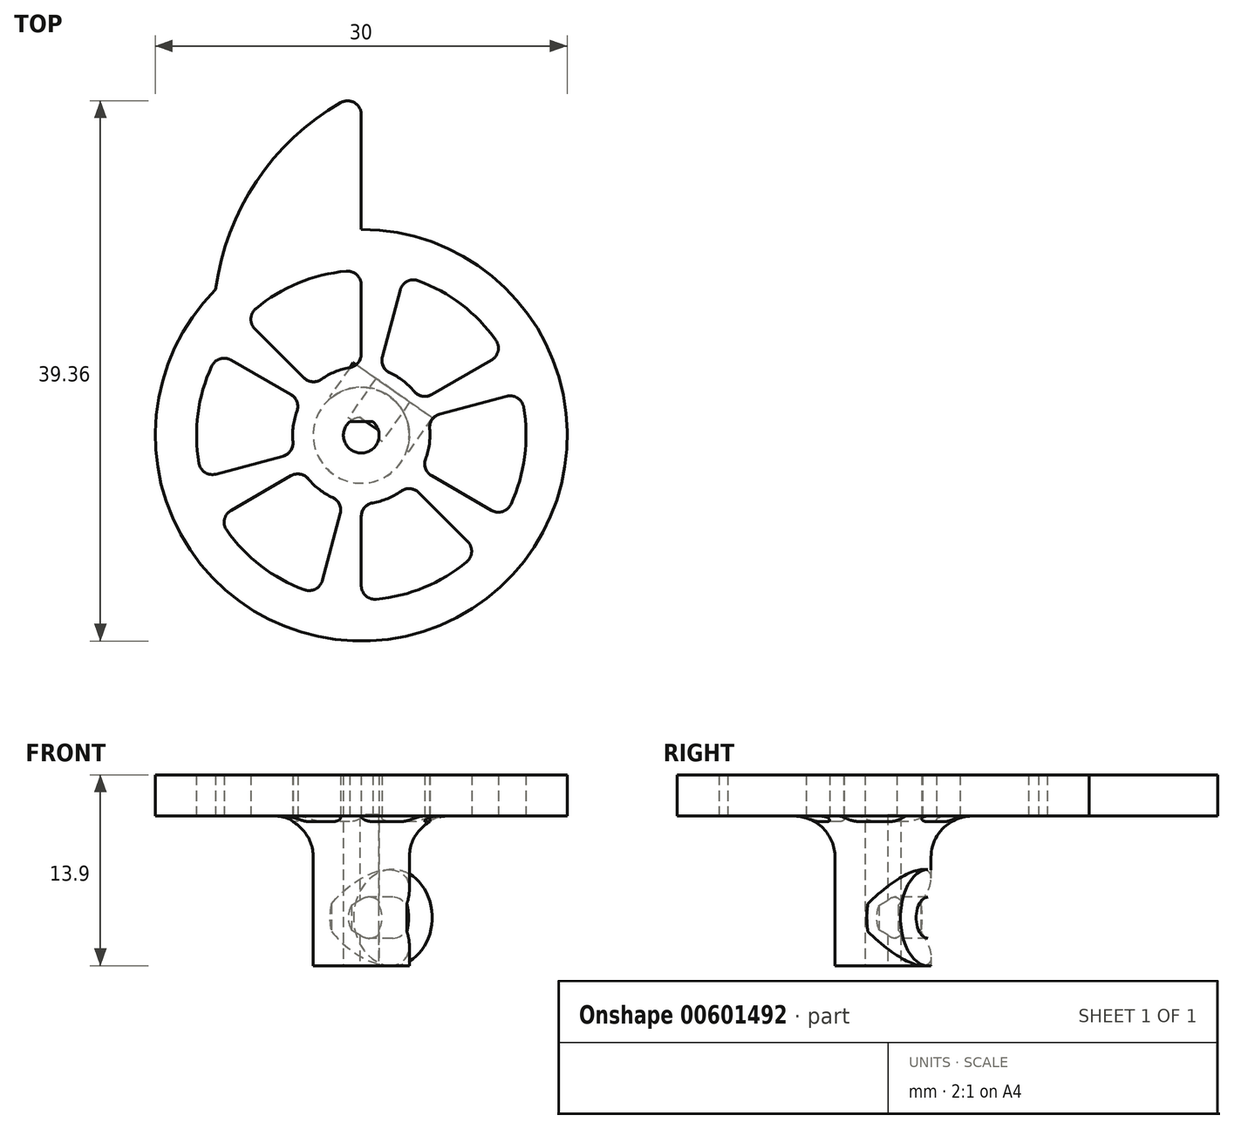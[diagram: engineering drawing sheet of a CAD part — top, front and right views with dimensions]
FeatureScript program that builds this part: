
annotation { "Feature Type Name" : "Feature", "Feature Type Description" : "" }
export const myFeature = defineFeature(function(context is Context, id is Id, definition is map)
    precondition{}
    {
        {
            assignVariable(context, id + "F0", {"name" : "shaftL", "anyValue" : 11});
        }
        {
            assignVariable(context, id + "F1", {"name" : "wheelThickness", "anyValue" : 3});
        }
        {
            var Q0;
            Q0=qCreatedBy(makeId("Top.planeOp"),FACE);
            var sketch = newSketch(context, id + "F2", { "sketchPlane" : qUnion([Q0])});
            skCircle(sketch, "E0", {"center": v(0, 0) * mm, "radius": 1.3 * mm});
            skLineSegment(sketch, "E1", {"start": v(0, 0) * mm, "end": v(0, 1) * mm, "construction": true});
            skLineSegment(sketch, "E2", {"start": v(0, 1) * mm, "end": v(0.83, 1) * mm});
            skLineSegment(sketch, "E3", {"start": v(0, 1) * mm, "end": v(-0.83, 1) * mm});
            skCircle(sketch, "E4", {"center": v(0, 0) * mm, "radius": 3.5 * mm});
            skSolve(sketch);
        }
        {
            var Q0;
            Q0=makeQuery(id+"F2.imprint","IMPRINT",FACE,{"disambiguationData":[TD([[makeQuery(id+"F2.imprint","IMPRINT",EDGE,{"derivedFrom":sQuery(id+"F2.wireOp",EDGE,"E4")}),1.0]])]});
            var Q1;
            {var subQ0=sQuery(id+"F2.wireOp",EDGE,"E2");Q1=makeQuery(id+"F2.imprint","IMPRINT",FACE,{"disambiguationData":[TD([[makeQuery(id+"F2.imprint","IMPRINT",EDGE,{"derivedFrom":subQ0}),1.0]])]});}
            extrude(context, id + "F3", {"entities" : qUnion([Q0, Q1]), "depth" : (getVariable(context, 'shaftL')) * mm, "offsetDistance" : 25 * mm});
        }
        {
            var Q0;
            Q0=makeQuery(id+"F3.opExtrude","SWEPT_FACE",FACE,{"disambiguationData":[OSD([sQuery(id+"F2.wireOp",EDGE,"E2"),sQuery(id+"F2.wireOp",EDGE,"E3")])]});
            var sketch = newSketch(context, id + "F4", { "sketchPlane" : qUnion([Q0])});
            skLineSegment(sketch, "E5", {"start": v(0, 0) * mm, "end": v(0, 11) * mm, "construction": true});
            skCircle(sketch, "E6", {"center": v(0, 3.5) * mm, "radius": 1.5 * mm});
            skCircle(sketch, "E7", {"center": v(0, 3.5) * mm, "radius": 3.5 * mm});
            skSolve(sketch);
        }
        {
            var Q0;
            {var subQ0=sQuery(id+"F4.wireOp",EDGE,"E6");var subQ1=sQuery(id+"F2.wireOp",EDGE,"E0");var subQ2=makeQuery(id+"F3.opExtrude","SWEPT_EDGE",EDGE,{"disambiguationData":[OSD([subQ1,sQuery(id+"F2.wireOp",EDGE,"E3")])]});var subQ3=makeQuery(id+"F4.imprint","INTERSECT",VERTEX,{"disambiguationData":[OD(0.0)],"derivedFrom":[subQ2,subQ0]});Q0=makeQuery(id+"F4.imprint","IMPRINT",FACE,{"disambiguationData":[TD([[makeQuery(id+"F4.imprint","IMPRINT",EDGE,{"disambiguationData":[TD([[subQ3,1.0]])],"derivedFrom":subQ0}),1.0]])]});}
            var Q1;
            {var subQ0=sQuery(id+"F4.wireOp",EDGE,"E6");var subQ1=makeQuery(id+"F3.opExtrude","SWEPT_EDGE",EDGE,{"disambiguationData":[OSD([sQuery(id+"F2.wireOp",EDGE,"E0"),sQuery(id+"F2.wireOp",EDGE,"E2")])]});var subQ2=makeQuery(id+"F4.imprint","INTERSECT",VERTEX,{"disambiguationData":[OD(0.0)],"derivedFrom":[subQ1,subQ0]});Q1=makeQuery(id+"F4.imprint","IMPRINT",FACE,{"disambiguationData":[TD([[makeQuery(id+"F4.imprint","IMPRINT",EDGE,{"disambiguationData":[TD([[subQ2,1.0]])],"derivedFrom":subQ0}),1.0]])]});}
            var Q2;
            {var subQ0=sQuery(id+"F4.wireOp",EDGE,"E6");var subQ1=makeQuery(id+"F3.opExtrude","SWEPT_EDGE",EDGE,{"disambiguationData":[OSD([sQuery(id+"F2.wireOp",EDGE,"E0"),sQuery(id+"F2.wireOp",EDGE,"E3")])]});var subQ2=makeQuery(id+"F4.imprint","INTERSECT",VERTEX,{"disambiguationData":[OD(0.0)],"derivedFrom":[subQ1,subQ0]});Q2=makeQuery(id+"F4.imprint","IMPRINT",FACE,{"disambiguationData":[TD([[makeQuery(id+"F4.imprint","IMPRINT",EDGE,{"disambiguationData":[TD([[subQ2,-1.0]])],"derivedFrom":subQ0}),1.0]])]});}
            var Q3;
            Q3=sQuery(id+"F4.wireOp",EDGE,"E6");
            extrude(context, id + "F5", {"entities" : qUnion([Q0, Q1, Q2]), "operationType" : NewBodyOperationType.REMOVE, "surfaceEntities" : qUnion([Q3]), "oppositeDirection" : true, "depth" : 25 * mm, "offsetDistance" : 25 * mm, "hasSecondDirection" : true, "secondDirectionOppositeDirection" : false, "secondDirectionDepth" : 0.5 * mm});
        }
        {
            var Q0;
            {var subQ0=sQuery(id+"F4.wireOp",EDGE,"E6");var subQ1=makeQuery(id+"F3.opExtrude","SWEPT_EDGE",EDGE,{"disambiguationData":[OSD([sQuery(id+"F2.wireOp",EDGE,"E0"),sQuery(id+"F2.wireOp",EDGE,"E3")])]});var subQ2=makeQuery(id+"F4.imprint","INTERSECT",VERTEX,{"disambiguationData":[OD(0.0)],"derivedFrom":[subQ1,subQ0]});Q0=makeQuery(id+"F4.imprint","IMPRINT",FACE,{"disambiguationData":[TD([[makeQuery(id+"F4.imprint","IMPRINT",EDGE,{"disambiguationData":[TD([[subQ2,-1.0]])],"derivedFrom":subQ0}),-1.0]])]});}
            var Q1;
            {var subQ2=sQuery(id+"F2.wireOp",EDGE,"E0");var subQ5=sQuery(id+"F4.wireOp",EDGE,"E6");var subQ7=sQuery(id+"F2.wireOp",EDGE,"E3");var subQ9=makeQuery(id+"F3.opExtrude","SWEPT_EDGE",EDGE,{"disambiguationData":[OSD([subQ2,subQ7])]});var subQ11=makeQuery(id+"F4.imprint","INTERSECT",VERTEX,{"disambiguationData":[OD(0.0)],"derivedFrom":[subQ9,subQ5]});Q1=makeQuery(id+"F4.imprint","IMPRINT",FACE,{"disambiguationData":[TD([[makeQuery(id+"F4.imprint","IMPRINT",EDGE,{"disambiguationData":[TD([[subQ11,1.0]])],"derivedFrom":subQ5}),-1.0]])]});}
            var Q2;
            {var subQ2=sQuery(id+"F2.wireOp",EDGE,"E0");var subQ5=sQuery(id+"F4.wireOp",EDGE,"E6");var subQ7=sQuery(id+"F2.wireOp",EDGE,"E3");var subQ9=makeQuery(id+"F3.opExtrude","SWEPT_EDGE",EDGE,{"disambiguationData":[OSD([subQ2,subQ7])]});var subQ11=makeQuery(id+"F4.imprint","INTERSECT",VERTEX,{"disambiguationData":[OD(1.0)],"derivedFrom":[subQ9,subQ5]});Q2=makeQuery(id+"F4.imprint","IMPRINT",FACE,{"disambiguationData":[TD([[makeQuery(id+"F4.imprint","IMPRINT",EDGE,{"disambiguationData":[TD([[subQ11,-1.0]])],"derivedFrom":subQ5}),-1.0]])]});}
            var Q3;
            {var subQ0=sQuery(id+"F4.wireOp",EDGE,"E6");var subQ1=makeQuery(id+"F3.opExtrude","SWEPT_EDGE",EDGE,{"disambiguationData":[OSD([sQuery(id+"F2.wireOp",EDGE,"E0"),sQuery(id+"F2.wireOp",EDGE,"E2")])]});var subQ2=makeQuery(id+"F4.imprint","INTERSECT",VERTEX,{"disambiguationData":[OD(0.0)],"derivedFrom":[subQ1,subQ0]});Q3=makeQuery(id+"F4.imprint","IMPRINT",FACE,{"disambiguationData":[TD([[makeQuery(id+"F4.imprint","IMPRINT",EDGE,{"disambiguationData":[TD([[subQ2,1.0]])],"derivedFrom":subQ0}),-1.0]])]});}
            extrude(context, id + "F6", {"entities" : qUnion([Q0, Q1, Q2, Q3]), "operationType" : NewBodyOperationType.ADD, "oppositeDirection" : true, "depth" : 3 * mm, "offsetDistance" : 25 * mm});
        }
        {
            var Q0;
            Q0=makeQuery(id+"F3.opExtrude","CAP_FACE",FACE,{"disambiguationData":[OSD([sQuery(id+"F2.wireOp",EDGE,"E0"),sQuery(id+"F2.wireOp",EDGE,"E2"),sQuery(id+"F2.wireOp",EDGE,"E3"),sQuery(id+"F2.wireOp",EDGE,"E4")])],"isStart":false});
            var sketch = newSketch(context, id + "F7", { "sketchPlane" : qUnion([Q0])});
            skCircle(sketch, "E8", {"center": v(0, 0) * mm, "radius": 15 * mm});
            skLineSegment(sketch, "E9", {"start": v(0, 15) * mm, "end": v(0, 25) * mm});
            skPoint(sketch, "E9.startSnap0", {"position": v(0, 1) * mm});
            skLineSegment(sketch, "E10", {"start": v(0, 0) * mm, "end": v(-5.74, 13.86) * mm, "construction": true});
            skLineSegment(sketch, "E11", {"start": v(-5.74, 13.86) * mm, "end": v(-7.65, 18.48) * mm});
            skLineSegment(sketch, "E12", {"start": v(0, 0) * mm, "end": v(-10.6, 10.6) * mm, "construction": true});
            skArc(sketch, "E13", {"start": v(0, 25) * mm, "mid": v(-7.16, 19.17) * mm, "end": v(-10.6, 10.6) * mm});
            skLineSegment(sketch, "E14", {"start": v(0, 0) * mm, "end": v(0, 15) * mm, "construction": true});
            skLineSegment(sketch, "E15", {"start": v(-5.74, 13.86) * mm, "end": v(-4.6, 11.09) * mm, "construction": true});
            skLineSegment(sketch, "E16", {"start": v(0, 0) * mm, "end": v(-1.91, 4.62) * mm});
            skLineSegment(sketch, "E17", {"start": v(0, 15) * mm, "end": v(0, 12) * mm, "construction": true});
            skLineSegment(sketch, "E18", {"start": v(-10.6, 10.6) * mm, "end": v(-8.49, 8.49) * mm, "construction": true});
            skLineSegment(sketch, "E19", {"start": v(0, 0) * mm, "end": v(-3.54, 3.54) * mm, "construction": true});
            skLineSegment(sketch, "E20", {"start": v(0, 0) * mm, "end": v(0, 5) * mm, "construction": true});
            skArc(sketch, "E21", {"start": v(-0.83, 4.93) * mm, "mid": v(-1.91, 4.62) * mm, "end": v(-2.9, 4.08) * mm});
            skArc(sketch, "E22", {"start": v(-1.1, 11.95) * mm, "mid": v(-4.6, 11.09) * mm, "end": v(-7.68, 9.22) * mm});
            skLineSegment(sketch, "E23", {"start": v(0, 10.95) * mm, "end": v(0, 5.92) * mm});
            skLineSegment(sketch, "E24", {"start": v(-7.75, 7.75) * mm, "end": v(-4.18, 4.18) * mm});
            skPoint(sketch, "E25.visualSharp", {"position": v(-8.49, 8.49) * mm});
            skArc(sketch, "E25.filletArc", {"start": v(-7.68, 9.22) * mm, "mid": v(-8.04, 8.5) * mm, "end": v(-7.75, 7.75) * mm});
            skPoint(sketch, "E26.visualSharp", {"position": v(0, 12) * mm});
            skArc(sketch, "E26.filletArc", {"start": v(0, 10.95) * mm, "mid": v(-0.33, 11.7) * mm, "end": v(-1.1, 11.95) * mm});
            skPoint(sketch, "E27.visualSharp", {"position": v(0, 5) * mm});
            skArc(sketch, "E27.filletArc", {"start": v(-0.83, 4.93) * mm, "mid": v(-0.24, 5.27) * mm, "end": v(0, 5.92) * mm});
            skPoint(sketch, "E28.visualSharp", {"position": v(-3.54, 3.54) * mm});
            skArc(sketch, "E28.filletArc", {"start": v(-4.18, 4.18) * mm, "mid": v(-3.56, 3.9) * mm, "end": v(-2.9, 4.08) * mm});
            skArc(sketch, "E29.1.0", {"start": v(-11.83, -2.04) * mm, "mid": v(-11.38, -2.71) * mm, "end": v(-10.58, -2.84) * mm});
            skArc(sketch, "E29.1.1", {"start": v(-5.71, -1.53) * mm, "mid": v(-5.15, -1.14) * mm, "end": v(-4.98, -0.47) * mm});
            skArc(sketch, "E29.1.2", {"start": v(-4.69, 1.74) * mm, "mid": v(-4.96, 0.65) * mm, "end": v(-4.98, -0.47) * mm});
            skLineSegment(sketch, "E29.1.3", {"start": v(-10.58, -2.84) * mm, "end": v(-5.71, -1.53) * mm});
            skPoint(sketch, "E29.1.4", {"position": v(-11.6, -3.1) * mm});
            skPoint(sketch, "E29.1.5", {"position": v(-4.33, 2.5) * mm});
            skArc(sketch, "E29.1.6", {"start": v(-4.69, 1.74) * mm, "mid": v(-4.68, 2.43) * mm, "end": v(-5.12, 2.96) * mm});
            skLineSegment(sketch, "E29.1.7", {"start": v(-9.49, 5.48) * mm, "end": v(-5.12, 2.96) * mm});
            skPoint(sketch, "E29.1.8", {"position": v(-10.4, 6) * mm});
            skArc(sketch, "E29.1.9", {"start": v(-9.49, 5.48) * mm, "mid": v(-10.29, 5.56) * mm, "end": v(-10.9, 5.03) * mm});
            skArc(sketch, "E29.1.10", {"start": v(-10.9, 5.03) * mm, "mid": v(-11.9, 1.57) * mm, "end": v(-11.83, -2.04) * mm});
            skArc(sketch, "E29.2.0", {"start": v(-4.15, -11.26) * mm, "mid": v(-3.34, -11.21) * mm, "end": v(-2.84, -10.58) * mm});
            skArc(sketch, "E29.2.1", {"start": v(-1.53, -5.71) * mm, "mid": v(-1.6, -5.03) * mm, "end": v(-2.08, -4.55) * mm});
            skArc(sketch, "E29.2.2", {"start": v(-3.85, -3.19) * mm, "mid": v(-3.04, -3.97) * mm, "end": v(-2.08, -4.55) * mm});
            skLineSegment(sketch, "E29.2.3", {"start": v(-2.84, -10.58) * mm, "end": v(-1.53, -5.71) * mm});
            skPoint(sketch, "E29.2.4", {"position": v(-3.1, -11.6) * mm});
            skPoint(sketch, "E29.2.5", {"position": v(-4.33, -2.5) * mm});
            skArc(sketch, "E29.2.6", {"start": v(-3.85, -3.19) * mm, "mid": v(-4.45, -2.84) * mm, "end": v(-5.12, -2.96) * mm});
            skLineSegment(sketch, "E29.2.7", {"start": v(-9.49, -5.48) * mm, "end": v(-5.12, -2.96) * mm});
            skPoint(sketch, "E29.2.8", {"position": v(-10.4, -6) * mm});
            skArc(sketch, "E29.2.9", {"start": v(-9.49, -5.48) * mm, "mid": v(-9.96, -6.13) * mm, "end": v(-9.8, -6.92) * mm});
            skArc(sketch, "E29.2.10", {"start": v(-9.8, -6.92) * mm, "mid": v(-7.3, -9.52) * mm, "end": v(-4.15, -11.26) * mm});
            skArc(sketch, "E29.3.0", {"start": v(7.68, -9.22) * mm, "mid": v(8.04, -8.5) * mm, "end": v(7.75, -7.75) * mm});
            skArc(sketch, "E29.3.1", {"start": v(4.18, -4.18) * mm, "mid": v(3.56, -3.9) * mm, "end": v(2.9, -4.08) * mm});
            skArc(sketch, "E29.3.2", {"start": v(0.83, -4.93) * mm, "mid": v(1.91, -4.62) * mm, "end": v(2.9, -4.08) * mm});
            skLineSegment(sketch, "E29.3.3", {"start": v(7.75, -7.75) * mm, "end": v(4.18, -4.18) * mm});
            skPoint(sketch, "E29.3.4", {"position": v(8.49, -8.49) * mm});
            skPoint(sketch, "E29.3.5", {"position": v(0, -5) * mm});
            skArc(sketch, "E29.3.6", {"start": v(0.83, -4.93) * mm, "mid": v(0.24, -5.27) * mm, "end": v(0, -5.92) * mm});
            skLineSegment(sketch, "E29.3.7", {"start": v(0, -10.95) * mm, "end": v(0, -5.92) * mm});
            skPoint(sketch, "E29.3.8", {"position": v(0, -12) * mm});
            skArc(sketch, "E29.3.9", {"start": v(0, -10.95) * mm, "mid": v(0.33, -11.7) * mm, "end": v(1.1, -11.95) * mm});
            skArc(sketch, "E29.3.10", {"start": v(1.1, -11.95) * mm, "mid": v(4.6, -11.09) * mm, "end": v(7.68, -9.22) * mm});
            skArc(sketch, "E29.4.0", {"start": v(11.83, 2.04) * mm, "mid": v(11.38, 2.71) * mm, "end": v(10.58, 2.84) * mm});
            skArc(sketch, "E29.4.1", {"start": v(5.71, 1.53) * mm, "mid": v(5.15, 1.14) * mm, "end": v(4.98, 0.47) * mm});
            skArc(sketch, "E29.4.2", {"start": v(4.69, -1.74) * mm, "mid": v(4.96, -0.65) * mm, "end": v(4.98, 0.47) * mm});
            skLineSegment(sketch, "E29.4.3", {"start": v(10.58, 2.84) * mm, "end": v(5.71, 1.53) * mm});
            skPoint(sketch, "E29.4.4", {"position": v(11.6, 3.1) * mm});
            skPoint(sketch, "E29.4.5", {"position": v(4.33, -2.5) * mm});
            skArc(sketch, "E29.4.6", {"start": v(4.69, -1.74) * mm, "mid": v(4.68, -2.43) * mm, "end": v(5.12, -2.96) * mm});
            skLineSegment(sketch, "E29.4.7", {"start": v(9.49, -5.48) * mm, "end": v(5.12, -2.96) * mm});
            skPoint(sketch, "E29.4.8", {"position": v(10.4, -6) * mm});
            skArc(sketch, "E29.4.9", {"start": v(9.49, -5.48) * mm, "mid": v(10.29, -5.56) * mm, "end": v(10.9, -5.03) * mm});
            skArc(sketch, "E29.4.10", {"start": v(10.9, -5.03) * mm, "mid": v(11.9, -1.57) * mm, "end": v(11.83, 2.04) * mm});
            skArc(sketch, "E29.5.0", {"start": v(4.15, 11.26) * mm, "mid": v(3.34, 11.21) * mm, "end": v(2.84, 10.58) * mm});
            skArc(sketch, "E29.5.1", {"start": v(1.53, 5.71) * mm, "mid": v(1.6, 5.03) * mm, "end": v(2.08, 4.55) * mm});
            skArc(sketch, "E29.5.2", {"start": v(3.85, 3.19) * mm, "mid": v(3.04, 3.97) * mm, "end": v(2.08, 4.55) * mm});
            skLineSegment(sketch, "E29.5.3", {"start": v(2.84, 10.58) * mm, "end": v(1.53, 5.71) * mm});
            skPoint(sketch, "E29.5.4", {"position": v(3.1, 11.6) * mm});
            skPoint(sketch, "E29.5.5", {"position": v(4.33, 2.5) * mm});
            skArc(sketch, "E29.5.6", {"start": v(3.85, 3.19) * mm, "mid": v(4.45, 2.84) * mm, "end": v(5.12, 2.96) * mm});
            skLineSegment(sketch, "E29.5.7", {"start": v(9.49, 5.48) * mm, "end": v(5.12, 2.96) * mm});
            skPoint(sketch, "E29.5.8", {"position": v(10.4, 6) * mm});
            skArc(sketch, "E29.5.9", {"start": v(9.49, 5.48) * mm, "mid": v(9.96, 6.13) * mm, "end": v(9.8, 6.92) * mm});
            skArc(sketch, "E29.5.10", {"start": v(9.8, 6.92) * mm, "mid": v(7.3, 9.52) * mm, "end": v(4.15, 11.26) * mm});
            skSolve(sketch);
        }
        {
            var Q0;
            {var subQ0=sQuery(id+"F7.wireOp",EDGE,"E9");Q0=makeQuery(id+"F7.imprint","IMPRINT",FACE,{"disambiguationData":[TD([[makeQuery(id+"F7.imprint","IMPRINT",EDGE,{"derivedFrom":subQ0}),1.0]])]});}
            var Q1;
            {var subQ0=sQuery(id+"F7.wireOp",EDGE,"E11");Q1=makeQuery(id+"F7.imprint","IMPRINT",FACE,{"disambiguationData":[TD([[makeQuery(id+"F7.imprint","IMPRINT",EDGE,{"derivedFrom":subQ0}),1.0]])]});}
            var Q2;
            Q2=makeQuery(id+"F7.imprint","IMPRINT",FACE,{"disambiguationData":[TD([[makeQuery(id+"F7.imprint","IMPRINT",EDGE,{"derivedFrom":makeQuery(id+"F3.opExtrude","CAP_EDGE",EDGE,{"disambiguationData":[OSD([sQuery(id+"F2.wireOp",EDGE,"E4")])],"isStart":false})}),-1.0]])]});
            var Q3;
            Q3=makeQuery(id+"F7.imprint","IMPRINT",FACE,{"disambiguationData":[TD([[makeQuery(id+"F7.imprint","IMPRINT",EDGE,{"derivedFrom":makeQuery(id+"F3.opExtrude","CAP_EDGE",EDGE,{"disambiguationData":[OSD([sQuery(id+"F2.wireOp",EDGE,"E0")])],"isStart":false})}),-1.0]])]});
            extrude(context, id + "F8", {"entities" : qUnion([Q0, Q1, Q2, Q3]), "depth" : (getVariable(context, 'wheelThickness')) * mm, "offsetDistance" : 25 * mm});
        }
        {
            var Q0;
            Q0=makeQuery(id+"F8.opExtrude","SWEPT_BODY",BODY,{"disambiguationData":[OSD([sQuery(id+"F2.wireOp",EDGE,"E0"),sQuery(id+"F2.wireOp",EDGE,"E2"),sQuery(id+"F2.wireOp",EDGE,"E3"),sQuery(id+"F7.wireOp",EDGE,"E8"),sQuery(id+"F7.wireOp",EDGE,"E9"),sQuery(id+"F7.wireOp",EDGE,"E13")])]});
            transform(context, id + "F9", {"entities" : qUnion([Q0]), "transformType" : TransformType.TRANSLATION_3D, "dx" : 0 * mm, "dy" : 0 * mm, "dz" : -0.1 * mm, "makeCopy" : false});
        }
        {
            var Q0;
            Q0=makeQuery(id+"F3.opExtrude","SWEPT_BODY",BODY,{"disambiguationData":[OSD([sQuery(id+"F2.wireOp",EDGE,"E0"),sQuery(id+"F2.wireOp",EDGE,"E2"),sQuery(id+"F2.wireOp",EDGE,"E3"),sQuery(id+"F2.wireOp",EDGE,"E4")])]});
            var Q1;
            Q1=makeQuery(id+"F3.opExtrude","SWEPT_FACE",FACE,{"disambiguationData":[OSD([sQuery(id+"F2.wireOp",EDGE,"E0")])]});
            transform(context, id + "F10", {"entities" : qUnion([Q0]), "transformType" : TransformType.ROTATION, "transformAxis" : qUnion([Q1]), "angle" : 35 * degree, "oppositeDirection" : true, "makeCopy" : false});
        }
        {
            var Q0;
            Q0=makeQuery(id+"F8.opExtrude","SWEPT_BODY",BODY,{"disambiguationData":[OSD([sQuery(id+"F2.wireOp",EDGE,"E0"),sQuery(id+"F2.wireOp",EDGE,"E2"),sQuery(id+"F2.wireOp",EDGE,"E3"),sQuery(id+"F7.wireOp",EDGE,"E8"),sQuery(id+"F7.wireOp",EDGE,"E9"),sQuery(id+"F7.wireOp",EDGE,"E13")])]});
            var Q1;
            Q1=makeQuery(id+"F3.opExtrude","SWEPT_BODY",BODY,{"disambiguationData":[OSD([sQuery(id+"F2.wireOp",EDGE,"E0"),sQuery(id+"F2.wireOp",EDGE,"E2"),sQuery(id+"F2.wireOp",EDGE,"E3"),sQuery(id+"F2.wireOp",EDGE,"E4")])]});
            booleanBodies(context, id + "F11", {"operationType" : BooleanOperationType.UNION, "tools" : qUnion([Q0, Q1])});
        }
        {
            var Q0;
            Q0=makeQuery(id+"F11.opBoolean","INTERSECT",EDGE,{"derivedFrom":[makeQuery(id+"F3.opExtrude","SWEPT_FACE",FACE,{"disambiguationData":[OSD([sQuery(id+"F2.wireOp",EDGE,"E4")])]}),makeQuery(id+"F8.opExtrude","CAP_FACE",FACE,{"disambiguationData":[OSD([sQuery(id+"F2.wireOp",EDGE,"E0"),sQuery(id+"F2.wireOp",EDGE,"E2"),sQuery(id+"F2.wireOp",EDGE,"E3"),sQuery(id+"F7.wireOp",EDGE,"E8"),sQuery(id+"F7.wireOp",EDGE,"E9"),sQuery(id+"F7.wireOp",EDGE,"E13")])],"isStart":true})]});
            fillet(context, id + "F12", {"entities" : qUnion([Q0]), "radius" : 3 * mm, "tangentPropagation" : true, "allowEdgeOverflow" : false});
        }
        {
            var Q0;
            Q0=makeQuery(id+"F8.opExtrude","SWEPT_EDGE",EDGE,{"disambiguationData":[OSD([sQuery(id+"F7.wireOp",EDGE,"E9"),sQuery(id+"F7.wireOp",EDGE,"E13")])]});
            fillet(context, id + "F13", {"entities" : qUnion([Q0]), "radius" : 1 * mm, "tangentPropagation" : true, "allowEdgeOverflow" : false});
        }
    });
